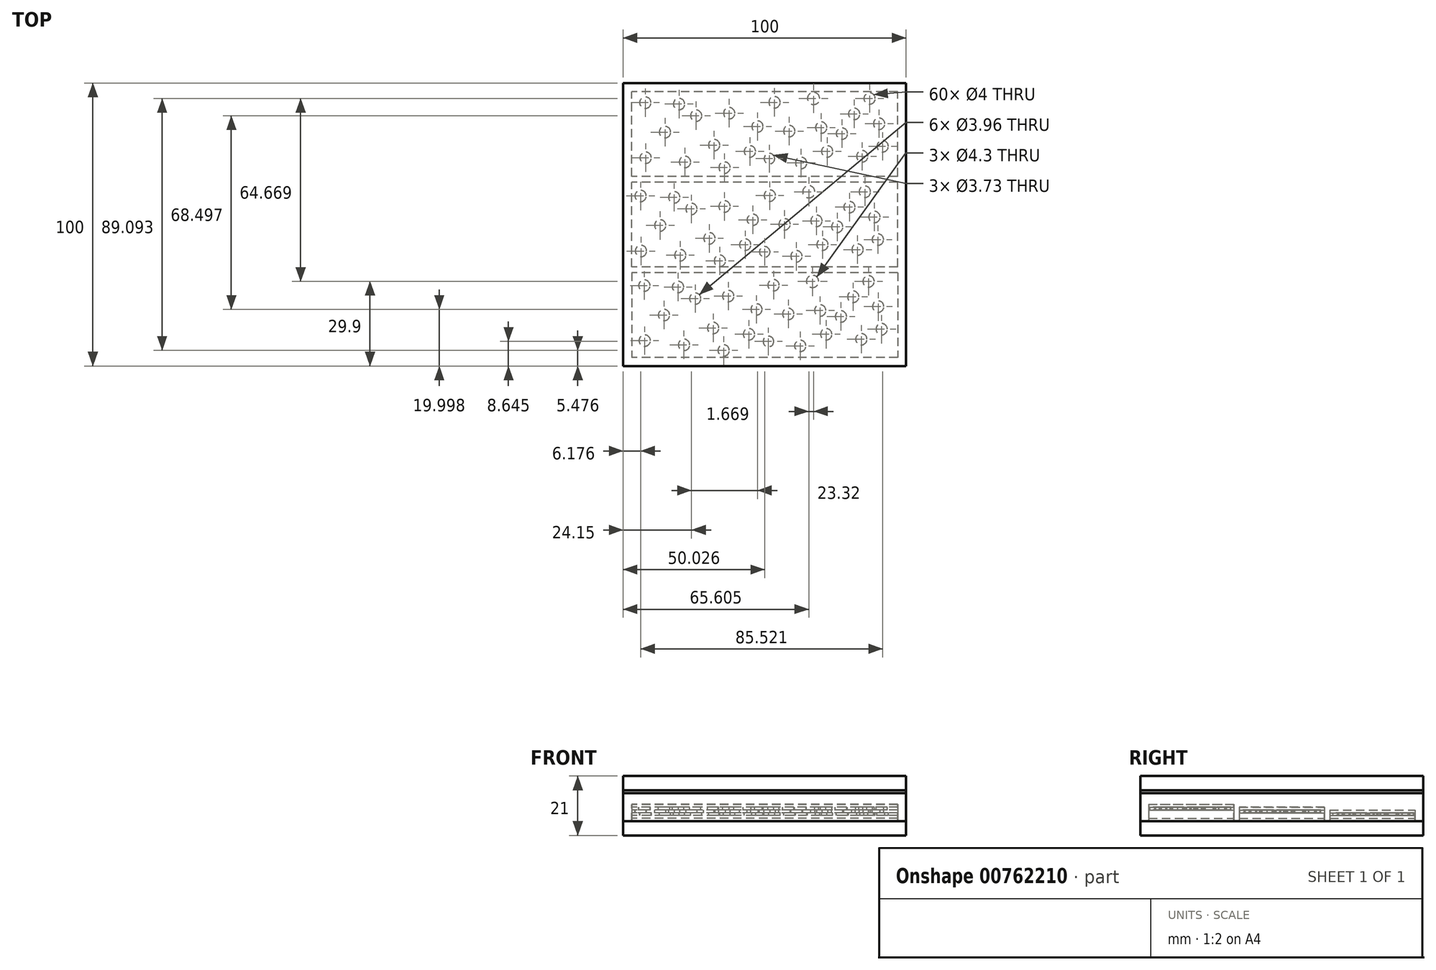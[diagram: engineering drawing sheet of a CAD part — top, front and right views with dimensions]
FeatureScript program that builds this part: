
annotation { "Feature Type Name" : "Feature", "Feature Type Description" : "" }
export const myFeature = defineFeature(function(context is Context, id is Id, definition is map)
    precondition{}
    {
        {
            var Q0;
            Q0=qCreatedBy(makeId("Top.planeOp"),FACE);
            var sketch = newSketch(context, id + "F0", { "sketchPlane" : qUnion([Q0])});
            skLineSegment(sketch, "E0.bottom", {"start": v(50, -50) * mm, "end": v(-50, -50) * mm});
            skLineSegment(sketch, "E0.top", {"start": v(50, 50) * mm, "end": v(-50, 50) * mm});
            skLineSegment(sketch, "E0.left", {"start": v(50, -50) * mm, "end": v(50, 50) * mm});
            skLineSegment(sketch, "E0.right", {"start": v(-50, -50) * mm, "end": v(-50, 50) * mm});
            skPoint(sketch, "E0.middle", {"position": v(0, 0) * mm});
            skSolve(sketch);
        }
        {
            var Q0;
            Q0=makeQuery(id+"F0.imprint","IMPRINT",FACE,{"disambiguationData":[TD([[makeQuery(id+"F0.imprint","IMPRINT",EDGE,{"derivedFrom":sQuery(id+"F0.wireOp",EDGE,"E0.bottom")}),-1.0]])]});
            extrude(context, id + "F1", {"entities" : qUnion([Q0]), "depth" : 5 * mm, "offsetDistance" : 25 * mm});
        }
        {
            var Q0;
            Q0=makeQuery(id+"F1.opExtrude","CAP_FACE",FACE,{"disambiguationData":[OSD([sQuery(id+"F0.wireOp",EDGE,"E0.bottom"),sQuery(id+"F0.wireOp",EDGE,"E0.top"),sQuery(id+"F0.wireOp",EDGE,"E0.left"),sQuery(id+"F0.wireOp",EDGE,"E0.right")])],"isStart":false});
            var sketch = newSketch(context, id + "F2", { "sketchPlane" : qUnion([Q0])});
            skLineSegment(sketch, "E1.bottom", {"start": v(47, -15) * mm, "end": v(-47, -15) * mm});
            skLineSegment(sketch, "E1.top", {"start": v(47, 15) * mm, "end": v(-47, 15) * mm});
            skLineSegment(sketch, "E1.left", {"start": v(47, -15) * mm, "end": v(47, 15) * mm});
            skLineSegment(sketch, "E1.right", {"start": v(-47, -15) * mm, "end": v(-47, 15) * mm});
            skPoint(sketch, "E1.middle", {"position": v(0, 0) * mm});
            skLineSegment(sketch, "E2.bottom", {"start": v(47, 17) * mm, "end": v(-47, 17) * mm});
            skLineSegment(sketch, "E2.top", {"start": v(47, 47) * mm, "end": v(-47, 47) * mm});
            skLineSegment(sketch, "E2.left", {"start": v(47, 17) * mm, "end": v(47, 47) * mm});
            skLineSegment(sketch, "E2.right", {"start": v(-47, 17) * mm, "end": v(-47, 47) * mm});
            skPoint(sketch, "E2.middle", {"position": v(0, 32) * mm});
            skLineSegment(sketch, "E3.bottom", {"start": v(47, -47) * mm, "end": v(-47, -47) * mm});
            skLineSegment(sketch, "E3.top", {"start": v(47, -17) * mm, "end": v(-47, -17) * mm});
            skLineSegment(sketch, "E3.left", {"start": v(47, -47) * mm, "end": v(47, -17) * mm});
            skLineSegment(sketch, "E3.right", {"start": v(-47, -47) * mm, "end": v(-47, -17) * mm});
            skPoint(sketch, "E3.middle", {"position": v(0, -32) * mm});
            skSolve(sketch);
        }
        {
            var Q0;
            Q0=makeQuery(id+"F2.imprint","IMPRINT",FACE,{"disambiguationData":[TD([[makeQuery(id+"F2.imprint","IMPRINT",EDGE,{"derivedFrom":sQuery(id+"F2.wireOp",EDGE,"E2.bottom")}),-1.0]])]});
            var Q1;
            Q1=makeQuery(id+"F2.imprint","IMPRINT",FACE,{"disambiguationData":[TD([[makeQuery(id+"F2.imprint","IMPRINT",EDGE,{"derivedFrom":sQuery(id+"F2.wireOp",EDGE,"E1.bottom")}),-1.0]])]});
            var Q2;
            Q2=makeQuery(id+"F2.imprint","IMPRINT",FACE,{"disambiguationData":[TD([[makeQuery(id+"F2.imprint","IMPRINT",EDGE,{"derivedFrom":sQuery(id+"F2.wireOp",EDGE,"E3.bottom")}),-1.0]])]});
            extrude(context, id + "F3", {"entities" : qUnion([Q0, Q1, Q2]), "depth" : 1 * mm, "offsetDistance" : 25 * mm});
        }
        {
            var Q0;
            Q0=makeQuery(id+"F3.opExtrude","CAP_FACE",FACE,{"disambiguationData":[OSD([sQuery(id+"F2.wireOp",EDGE,"E2.bottom"),sQuery(id+"F2.wireOp",EDGE,"E2.top"),sQuery(id+"F2.wireOp",EDGE,"E2.left"),sQuery(id+"F2.wireOp",EDGE,"E2.right")])],"isStart":false});
            extrude(context, id + "F4", {"entities" : qUnion([Q0]), "depth" : 1 * mm, "offsetDistance" : 25 * mm});
        }
        {
            var Q0;
            Q0=makeQuery(id+"F3.opExtrude","CAP_FACE",FACE,{"disambiguationData":[OSD([sQuery(id+"F2.wireOp",EDGE,"E1.bottom"),sQuery(id+"F2.wireOp",EDGE,"E1.top"),sQuery(id+"F2.wireOp",EDGE,"E1.left"),sQuery(id+"F2.wireOp",EDGE,"E1.right")])],"isStart":false});
            extrude(context, id + "F5", {"entities" : qUnion([Q0]), "depth" : 2 * mm, "offsetDistance" : 25 * mm});
        }
        {
            var Q0;
            Q0=makeQuery(id+"F3.opExtrude","CAP_FACE",FACE,{"disambiguationData":[OSD([sQuery(id+"F2.wireOp",EDGE,"E3.bottom"),sQuery(id+"F2.wireOp",EDGE,"E3.top"),sQuery(id+"F2.wireOp",EDGE,"E3.left"),sQuery(id+"F2.wireOp",EDGE,"E3.right")])],"isStart":false});
            extrude(context, id + "F6", {"entities" : qUnion([Q0]), "depth" : 3 * mm, "offsetDistance" : 25 * mm});
        }
        {
            var Q0;
            Q0=makeQuery(id+"F6.opExtrude","CAP_FACE",FACE,{"disambiguationData":[OSD([sQuery(id+"F2.wireOp",EDGE,"E3.bottom"),sQuery(id+"F2.wireOp",EDGE,"E3.top"),sQuery(id+"F2.wireOp",EDGE,"E3.left"),sQuery(id+"F2.wireOp",EDGE,"E3.right")])],"isStart":false});
            var Q1;
            Q1=makeQuery(id+"F5.opExtrude","CAP_FACE",FACE,{"disambiguationData":[OSD([sQuery(id+"F2.wireOp",EDGE,"E1.bottom"),sQuery(id+"F2.wireOp",EDGE,"E1.top"),sQuery(id+"F2.wireOp",EDGE,"E1.left"),sQuery(id+"F2.wireOp",EDGE,"E1.right")])],"isStart":false});
            var Q2;
            Q2=makeQuery(id+"F4.opExtrude","CAP_FACE",FACE,{"disambiguationData":[OSD([sQuery(id+"F2.wireOp",EDGE,"E2.bottom"),sQuery(id+"F2.wireOp",EDGE,"E2.top"),sQuery(id+"F2.wireOp",EDGE,"E2.left"),sQuery(id+"F2.wireOp",EDGE,"E2.right")])],"isStart":false});
            extrude(context, id + "F7", {"entities" : qUnion([Q0, Q1, Q2]), "depth" : 1 * mm, "offsetDistance" : 25 * mm});
        }
        {
            var Q0;
            Q0=makeQuery(id+"F7.opExtrude","CAP_FACE",FACE,{"disambiguationData":[OSD([sQuery(id+"F2.wireOp",EDGE,"E3.bottom"),sQuery(id+"F2.wireOp",EDGE,"E3.top"),sQuery(id+"F2.wireOp",EDGE,"E3.left"),sQuery(id+"F2.wireOp",EDGE,"E3.right")])],"isStart":false});
            var sketch = newSketch(context, id + "F8", { "sketchPlane" : qUnion([Q0])});
            skCircle(sketch, "E4", {"center": v(-35.55, -32) * mm, "radius": 2 * mm});
            skCircle(sketch, "E5", {"center": v(-18.19, -36.58) * mm, "radius": 2 * mm});
            skCircle(sketch, "E6", {"center": v(-12.85, -25.3) * mm, "radius": 2 * mm});
            skCircle(sketch, "E7", {"center": v(8.36, -31.62) * mm, "radius": 2 * mm});
            skCircle(sketch, "E8", {"center": v(19.64, -30.38) * mm, "radius": 2 * mm});
            skCircle(sketch, "E9", {"center": v(31.3, -25.54) * mm, "radius": 2 * mm});
            skCircle(sketch, "E10", {"center": v(34.16, -40.55) * mm, "radius": 2 * mm});
            skCircle(sketch, "E11", {"center": v(12.57, -42.9) * mm, "radius": 2 * mm});
            skCircle(sketch, "E12", {"center": v(3.15, -21.45) * mm, "radius": 2 * mm});
            skCircle(sketch, "E13", {"center": v(-5.53, -38.81) * mm, "radius": 2 * mm});
            skCircle(sketch, "E14", {"center": v(-30.59, -22.07) * mm, "radius": 2 * mm});
            skCircle(sketch, "E15", {"center": v(-42.37, -41.05) * mm, "radius": 2 * mm});
            skCircle(sketch, "E16", {"center": v(40.11, -29.01) * mm, "radius": 2 * mm});
            skCircle(sketch, "E17", {"center": v(-28.48, -42.53) * mm, "radius": 2 * mm});
            skCircle(sketch, "E18", {"center": v(21.75, -38.81) * mm, "radius": 2 * mm});
            skCircle(sketch, "E19", {"center": v(-42.5, -21.57) * mm, "radius": 2 * mm});
            skCircle(sketch, "E20", {"center": v(-2.87, -30) * mm, "radius": 1.98 * mm});
            skCircle(sketch, "E21", {"center": v(16.93, -20.1) * mm, "radius": 2.15 * mm});
            skCircle(sketch, "E22", {"center": v(-24.52, -26.17) * mm, "radius": 1.98 * mm});
            skCircle(sketch, "E23", {"center": v(36.73, -20.1) * mm, "radius": 2 * mm});
            skCircle(sketch, "E24", {"center": v(41.36, -37) * mm, "radius": 2 * mm});
            skCircle(sketch, "E25", {"center": v(26.97, -32.5) * mm, "radius": 2 * mm});
            skCircle(sketch, "E26", {"center": v(1.35, -41.36) * mm, "radius": 1.87 * mm});
            skCircle(sketch, "E27", {"center": v(-14.49, -44.52) * mm, "radius": 2 * mm});
            skSolve(sketch);
        }
        {
            var Q0;
            Q0 = qSketchRegion(id + "F8", true);
            extrude(context, id + "F9", {"entities" : qUnion([Q0]), "operationType" : NewBodyOperationType.REMOVE, "oppositeDirection" : true, "depth" : 1 * mm, "offsetDistance" : 25 * mm});
        }
        {
            var Q0;
            Q0=makeQuery(id+"F7.opExtrude","CAP_FACE",FACE,{"disambiguationData":[OSD([sQuery(id+"F2.wireOp",EDGE,"E1.bottom"),sQuery(id+"F2.wireOp",EDGE,"E1.top"),sQuery(id+"F2.wireOp",EDGE,"E1.left"),sQuery(id+"F2.wireOp",EDGE,"E1.right")])],"isStart":false});
            var sketch = newSketch(context, id + "F10", { "sketchPlane" : qUnion([Q0])});
            skCircle(sketch, "E28", {"center": v(-36.88, -0.3) * mm, "radius": 2 * mm});
            skCircle(sketch, "E29", {"center": v(-19.51, -4.9) * mm, "radius": 2 * mm});
            skCircle(sketch, "E30", {"center": v(-14.18, 6.4) * mm, "radius": 2 * mm});
            skCircle(sketch, "E31", {"center": v(7.03, 0.07) * mm, "radius": 2 * mm});
            skCircle(sketch, "E32", {"center": v(18.32, 1.3) * mm, "radius": 2 * mm});
            skCircle(sketch, "E33", {"center": v(29.98, 6.15) * mm, "radius": 2 * mm});
            skCircle(sketch, "E34", {"center": v(32.83, -8.86) * mm, "radius": 2 * mm});
            skCircle(sketch, "E35", {"center": v(11.25, -11.22) * mm, "radius": 2 * mm});
            skCircle(sketch, "E36", {"center": v(1.82, 10.24) * mm, "radius": 2 * mm});
            skCircle(sketch, "E37", {"center": v(-6.86, -7.13) * mm, "radius": 2 * mm});
            skCircle(sketch, "E38", {"center": v(-31.92, 9.62) * mm, "radius": 2 * mm});
            skCircle(sketch, "E39", {"center": v(-43.7, -9.36) * mm, "radius": 2 * mm});
            skCircle(sketch, "E40", {"center": v(38.78, 2.67) * mm, "radius": 2 * mm});
            skCircle(sketch, "E41", {"center": v(-29.8, -10.85) * mm, "radius": 2 * mm});
            skCircle(sketch, "E42", {"center": v(20.43, -7.13) * mm, "radius": 2 * mm});
            skCircle(sketch, "E43", {"center": v(-43.82, 10.12) * mm, "radius": 2 * mm});
            skCircle(sketch, "E44", {"center": v(-4.2, 1.69) * mm, "radius": 1.98 * mm});
            skCircle(sketch, "E45", {"center": v(15.6, 11.59) * mm, "radius": 2.15 * mm});
            skCircle(sketch, "E46", {"center": v(-25.85, 5.52) * mm, "radius": 1.98 * mm});
            skCircle(sketch, "E47", {"center": v(35.4, 11.59) * mm, "radius": 2 * mm});
            skCircle(sketch, "E48", {"center": v(40.03, -5.31) * mm, "radius": 2 * mm});
            skCircle(sketch, "E49", {"center": v(25.64, -0.82) * mm, "radius": 2 * mm});
            skCircle(sketch, "E50", {"center": v(0.03, -9.67) * mm, "radius": 1.87 * mm});
            skCircle(sketch, "E51", {"center": v(-15.82, -12.84) * mm, "radius": 2 * mm});
            skSolve(sketch);
        }
        {
            var Q0;
            Q0 = qSketchRegion(id + "F10", true);
            extrude(context, id + "F11", {"entities" : qUnion([Q0]), "operationType" : NewBodyOperationType.REMOVE, "oppositeDirection" : true, "depth" : 1 * mm, "offsetDistance" : 25 * mm});
        }
        {
            var Q0;
            Q0=makeQuery(id+"F7.opExtrude","CAP_FACE",FACE,{"disambiguationData":[OSD([sQuery(id+"F2.wireOp",EDGE,"E2.bottom"),sQuery(id+"F2.wireOp",EDGE,"E2.top"),sQuery(id+"F2.wireOp",EDGE,"E2.left"),sQuery(id+"F2.wireOp",EDGE,"E2.right")])],"isStart":false});
            var sketch = newSketch(context, id + "F12", { "sketchPlane" : qUnion([Q0])});
            skCircle(sketch, "E52", {"center": v(-35.2, 32.68) * mm, "radius": 2 * mm});
            skCircle(sketch, "E53", {"center": v(-17.84, 28.09) * mm, "radius": 2 * mm});
            skCircle(sketch, "E54", {"center": v(-12.51, 39.38) * mm, "radius": 2 * mm});
            skCircle(sketch, "E55", {"center": v(8.7, 33.05) * mm, "radius": 2 * mm});
            skCircle(sketch, "E56", {"center": v(19.99, 34.29) * mm, "radius": 2 * mm});
            skCircle(sketch, "E57", {"center": v(31.65, 39.13) * mm, "radius": 2 * mm});
            skCircle(sketch, "E58", {"center": v(34.5, 24.12) * mm, "radius": 2 * mm});
            skCircle(sketch, "E59", {"center": v(12.92, 21.76) * mm, "radius": 2 * mm});
            skCircle(sketch, "E60", {"center": v(3.49, 43.22) * mm, "radius": 2 * mm});
            skCircle(sketch, "E61", {"center": v(-5.2, 25.86) * mm, "radius": 2 * mm});
            skCircle(sketch, "E62", {"center": v(-30.25, 42.6) * mm, "radius": 2 * mm});
            skCircle(sketch, "E63", {"center": v(-42.03, 23.62) * mm, "radius": 2 * mm});
            skCircle(sketch, "E64", {"center": v(40.45, 35.65) * mm, "radius": 2 * mm});
            skCircle(sketch, "E65", {"center": v(-28.14, 22.13) * mm, "radius": 2 * mm});
            skCircle(sketch, "E66", {"center": v(22.1, 25.86) * mm, "radius": 2 * mm});
            skCircle(sketch, "E67", {"center": v(-42.16, 43.1) * mm, "radius": 2 * mm});
            skCircle(sketch, "E68", {"center": v(-2.53, 34.67) * mm, "radius": 1.98 * mm});
            skCircle(sketch, "E69", {"center": v(17.27, 44.57) * mm, "radius": 2.15 * mm});
            skCircle(sketch, "E70", {"center": v(-24.18, 38.5) * mm, "radius": 1.98 * mm});
            skCircle(sketch, "E71", {"center": v(37.08, 44.57) * mm, "radius": 2 * mm});
            skCircle(sketch, "E72", {"center": v(41.7, 27.67) * mm, "radius": 2 * mm});
            skCircle(sketch, "E73", {"center": v(27.3, 32.16) * mm, "radius": 2 * mm});
            skCircle(sketch, "E74", {"center": v(1.7, 23.31) * mm, "radius": 1.87 * mm});
            skCircle(sketch, "E75", {"center": v(-14.15, 20.14) * mm, "radius": 2 * mm});
            skSolve(sketch);
        }
        {
            var Q0;
            Q0 = qSketchRegion(id + "F12", true);
            extrude(context, id + "F13", {"entities" : qUnion([Q0]), "operationType" : NewBodyOperationType.REMOVE, "oppositeDirection" : true, "depth" : 1 * mm, "offsetDistance" : 25 * mm});
        }
        {
            var Q0;
            Q0=makeQuery(id+"F7.opExtrude","CAP_FACE",FACE,{"disambiguationData":[OSD([sQuery(id+"F2.wireOp",EDGE,"E2.bottom"),sQuery(id+"F2.wireOp",EDGE,"E2.top"),sQuery(id+"F2.wireOp",EDGE,"E2.left"),sQuery(id+"F2.wireOp",EDGE,"E2.right")])],"isStart":false});
            var sketch = newSketch(context, id + "F14", { "sketchPlane" : qUnion([Q0])});
            skLineSegment(sketch, "E76.bottom", {"start": v(47, 17) * mm, "end": v(-47, 17) * mm});
            skLineSegment(sketch, "E76.top", {"start": v(47, 47) * mm, "end": v(-47, 47) * mm});
            skLineSegment(sketch, "E76.left", {"start": v(47, 17) * mm, "end": v(47, 47) * mm});
            skLineSegment(sketch, "E76.right", {"start": v(-47, 17) * mm, "end": v(-47, 47) * mm});
            skPoint(sketch, "E76.middle", {"position": v(0, 32) * mm});
            skSolve(sketch);
        }
        {
            var Q0;
            Q0 = qSketchRegion(id + "F14", true);
            extrude(context, id + "F15", {"entities" : qUnion([Q0]), "depth" : 1 * mm, "offsetDistance" : 25 * mm});
        }
        {
            var Q0;
            Q0=makeQuery(id+"F7.opExtrude","CAP_FACE",FACE,{"disambiguationData":[OSD([sQuery(id+"F2.wireOp",EDGE,"E1.bottom"),sQuery(id+"F2.wireOp",EDGE,"E1.top"),sQuery(id+"F2.wireOp",EDGE,"E1.left"),sQuery(id+"F2.wireOp",EDGE,"E1.right")])],"isStart":false});
            var sketch = newSketch(context, id + "F16", { "sketchPlane" : qUnion([Q0])});
            skLineSegment(sketch, "E77.bottom", {"start": v(-47, -15) * mm, "end": v(47, -15) * mm});
            skLineSegment(sketch, "E77.top", {"start": v(-47, 15) * mm, "end": v(47, 15) * mm});
            skLineSegment(sketch, "E77.left", {"start": v(-47, -15) * mm, "end": v(-47, 15) * mm});
            skLineSegment(sketch, "E77.right", {"start": v(47, -15) * mm, "end": v(47, 15) * mm});
            skPoint(sketch, "E77.middle", {"position": v(0, 0) * mm});
            skSolve(sketch);
        }
        {
            var Q0;
            Q0 = qSketchRegion(id + "F16", true);
            extrude(context, id + "F17", {"entities" : qUnion([Q0]), "depth" : 1 * mm, "offsetDistance" : 25 * mm});
        }
        {
            var Q0;
            Q0=makeQuery(id+"F7.opExtrude","CAP_FACE",FACE,{"disambiguationData":[OSD([sQuery(id+"F2.wireOp",EDGE,"E3.bottom"),sQuery(id+"F2.wireOp",EDGE,"E3.top"),sQuery(id+"F2.wireOp",EDGE,"E3.left"),sQuery(id+"F2.wireOp",EDGE,"E3.right")])],"isStart":false});
            var sketch = newSketch(context, id + "F18", { "sketchPlane" : qUnion([Q0])});
            skLineSegment(sketch, "E78.bottom", {"start": v(47, -47) * mm, "end": v(-47, -47) * mm});
            skLineSegment(sketch, "E78.top", {"start": v(47, -17) * mm, "end": v(-47, -17) * mm});
            skLineSegment(sketch, "E78.left", {"start": v(47, -47) * mm, "end": v(47, -17) * mm});
            skLineSegment(sketch, "E78.right", {"start": v(-47, -47) * mm, "end": v(-47, -17) * mm});
            skPoint(sketch, "E78.middle", {"position": v(0, -32) * mm});
            skSolve(sketch);
        }
        {
            var Q0;
            Q0 = qSketchRegion(id + "F18", true);
            extrude(context, id + "F19", {"entities" : qUnion([Q0]), "depth" : 1 * mm, "offsetDistance" : 25 * mm});
        }
        {
            var Q0;
            Q0=makeQuery(id+"F15.opExtrude","SWEPT_FACE",FACE,{"disambiguationData":[OSD([sQuery(id+"F14.wireOp",EDGE,"E76.right")])]});
            var sketch = newSketch(context, id + "F20", { "sketchPlane" : qUnion([Q0])});
            skLineSegment(sketch, "E79", {"start": v(-50, 5) * mm, "end": v(-47, 5) * mm});
            skLineSegment(sketch, "E80", {"start": v(-47, 5) * mm, "end": v(-47, 8.94) * mm});
            skLineSegment(sketch, "E81", {"start": v(-47, 8.94) * mm, "end": v(-17, 8.94) * mm});
            skLineSegment(sketch, "E82", {"start": v(-17, 8.94) * mm, "end": v(-17, 5) * mm});
            skLineSegment(sketch, "E83", {"start": v(-17, 5) * mm, "end": v(-15, 5) * mm});
            skLineSegment(sketch, "E84", {"start": v(-15, 5) * mm, "end": v(-15, 10.02) * mm});
            skLineSegment(sketch, "E85", {"start": v(-15, 10.02) * mm, "end": v(15, 10.02) * mm});
            skLineSegment(sketch, "E86", {"start": v(15, 10.02) * mm, "end": v(15, 5) * mm});
            skLineSegment(sketch, "E87", {"start": v(15, 5) * mm, "end": v(17, 5) * mm});
            skLineSegment(sketch, "E88", {"start": v(17, 5) * mm, "end": v(17, 10.88) * mm});
            skLineSegment(sketch, "E89", {"start": v(17, 10.88) * mm, "end": v(47, 10.88) * mm});
            skLineSegment(sketch, "E90", {"start": v(47, 10.88) * mm, "end": v(47, 5) * mm});
            skLineSegment(sketch, "E91", {"start": v(47, 5) * mm, "end": v(50, 5) * mm});
            skLineSegment(sketch, "E92", {"start": v(50, 5) * mm, "end": v(50, 15) * mm});
            skLineSegment(sketch, "E93", {"start": v(50, 15) * mm, "end": v(-50, 15) * mm});
            skLineSegment(sketch, "E94", {"start": v(-50, 15) * mm, "end": v(-50, 5) * mm});
            skSolve(sketch);
        }
        {
            var Q0;
            {var subQ8=sQuery(id+"F20.wireOp",EDGE,"E79");Q0=makeQuery(id+"F20.imprint","IMPRINT",FACE,{"disambiguationData":[TD([[makeQuery(id+"F20.imprint","IMPRINT",EDGE,{"derivedFrom":subQ8}),1.0]])]});}
            extrude(context, id + "F21", {"entities" : qUnion([Q0]), "oppositeDirection" : true, "depth" : 94 * mm, "offsetDistance" : 25 * mm});
        }
        {
            var Q0;
            Q0=makeQuery(id+"F1.opExtrude","CAP_FACE",FACE,{"disambiguationData":[OSD([sQuery(id+"F0.wireOp",EDGE,"E0.bottom"),sQuery(id+"F0.wireOp",EDGE,"E0.top"),sQuery(id+"F0.wireOp",EDGE,"E0.left"),sQuery(id+"F0.wireOp",EDGE,"E0.right")])],"isStart":false});
            var sketch = newSketch(context, id + "F22", { "sketchPlane" : qUnion([Q0])});
            skLineSegment(sketch, "E95.bottom", {"start": v(-50, 50) * mm, "end": v(-47, 50) * mm});
            skLineSegment(sketch, "E95.top", {"start": v(-50, -50) * mm, "end": v(-47, -50) * mm});
            skLineSegment(sketch, "E95.left", {"start": v(-50, 50) * mm, "end": v(-50, -50) * mm});
            skLineSegment(sketch, "E95.right", {"start": v(-47, 50) * mm, "end": v(-47, -50) * mm});
            skLineSegment(sketch, "E96.bottom", {"start": v(47, 50) * mm, "end": v(50, 50) * mm});
            skLineSegment(sketch, "E96.top", {"start": v(47, -50) * mm, "end": v(50, -50) * mm});
            skLineSegment(sketch, "E96.left", {"start": v(47, 50) * mm, "end": v(47, -50) * mm});
            skLineSegment(sketch, "E96.right", {"start": v(50, 50) * mm, "end": v(50, -50) * mm});
            skSolve(sketch);
        }
        {
            var Q0;
            Q0=makeQuery(id+"F22.imprint","IMPRINT",FACE,{"disambiguationData":[TD([[makeQuery(id+"F22.imprint","IMPRINT",EDGE,{"derivedFrom":sQuery(id+"F22.wireOp",EDGE,"E95.bottom")}),1.0]])]});
            var Q1;
            Q1=makeQuery(id+"F22.imprint","IMPRINT",FACE,{"disambiguationData":[TD([[makeQuery(id+"F22.imprint","IMPRINT",EDGE,{"derivedFrom":sQuery(id+"F22.wireOp",EDGE,"E96.bottom")}),1.0]])]});
            extrude(context, id + "F23", {"entities" : qUnion([Q0, Q1]), "depth" : 10 * mm, "offsetDistance" : 25 * mm});
        }
        {
            var Q0;
            Q0=makeQuery(id+"F21.opExtrude","SWEPT_BODY",BODY,{"disambiguationData":[OSD([sQuery(id+"F14.wireOp",EDGE,"E76.bottom"),sQuery(id+"F14.wireOp",EDGE,"E76.top"),sQuery(id+"F14.wireOp",EDGE,"E76.right"),sQuery(id+"F20.wireOp",EDGE,"E79"),sQuery(id+"F20.wireOp",EDGE,"E80"),sQuery(id+"F20.wireOp",EDGE,"E82"),sQuery(id+"F20.wireOp",EDGE,"E83"),sQuery(id+"F20.wireOp",EDGE,"E84"),sQuery(id+"F20.wireOp",EDGE,"E85"),sQuery(id+"F20.wireOp",EDGE,"E86"),sQuery(id+"F20.wireOp",EDGE,"E87"),sQuery(id+"F20.wireOp",EDGE,"E88"),sQuery(id+"F20.wireOp",EDGE,"E89"),sQuery(id+"F20.wireOp",EDGE,"E90"),sQuery(id+"F20.wireOp",EDGE,"E91"),sQuery(id+"F20.wireOp",EDGE,"E92"),sQuery(id+"F20.wireOp",EDGE,"E93"),sQuery(id+"F20.wireOp",EDGE,"E94")])]});
            var Q1;
            Q1=makeQuery(id+"F23.opExtrude","SWEPT_BODY",BODY,{"disambiguationData":[OSD([sQuery(id+"F22.wireOp",EDGE,"E95.bottom"),sQuery(id+"F22.wireOp",EDGE,"E95.top"),sQuery(id+"F22.wireOp",EDGE,"E95.left"),sQuery(id+"F22.wireOp",EDGE,"E95.right")])]});
            var Q2;
            Q2=makeQuery(id+"F23.opExtrude","SWEPT_BODY",BODY,{"disambiguationData":[OSD([sQuery(id+"F22.wireOp",EDGE,"E96.bottom"),sQuery(id+"F22.wireOp",EDGE,"E96.top"),sQuery(id+"F22.wireOp",EDGE,"E96.left"),sQuery(id+"F22.wireOp",EDGE,"E96.right")])]});
            booleanBodies(context, id + "F24", {"operationType" : BooleanOperationType.UNION, "tools" : qUnion([Q0, Q1, Q2])});
        }
        {
            var Q0;
            Q0=makeQuery(id+"F24.opBoolean","MERGE",FACE,{"derivedFrom":[makeQuery(id+"F21.opExtrude","SWEPT_FACE",FACE,{"disambiguationData":[OSD([sQuery(id+"F20.wireOp",EDGE,"E93")])]}),makeQuery(id+"F23.opExtrude","CAP_FACE",FACE,{"disambiguationData":[OSD([sQuery(id+"F22.wireOp",EDGE,"E95.bottom"),sQuery(id+"F22.wireOp",EDGE,"E95.top"),sQuery(id+"F22.wireOp",EDGE,"E95.left"),sQuery(id+"F22.wireOp",EDGE,"E95.right")])],"isStart":false}),makeQuery(id+"F23.opExtrude","CAP_FACE",FACE,{"disambiguationData":[OSD([sQuery(id+"F22.wireOp",EDGE,"E96.bottom"),sQuery(id+"F22.wireOp",EDGE,"E96.top"),sQuery(id+"F22.wireOp",EDGE,"E96.left"),sQuery(id+"F22.wireOp",EDGE,"E96.right")])],"isStart":false})]});
            extrude(context, id + "F25", {"entities" : qUnion([Q0]), "depth" : 1 * mm, "offsetDistance" : 25 * mm});
        }
        {
            var Q0;
            Q0=makeQuery(id+"F25.opExtrude","CAP_FACE",FACE,{"disambiguationData":[OSD([sQuery(id+"F20.wireOp",EDGE,"E93"),sQuery(id+"F22.wireOp",EDGE,"E95.bottom"),sQuery(id+"F22.wireOp",EDGE,"E95.top"),sQuery(id+"F22.wireOp",EDGE,"E95.left"),sQuery(id+"F22.wireOp",EDGE,"E95.right"),sQuery(id+"F22.wireOp",EDGE,"E96.bottom"),sQuery(id+"F22.wireOp",EDGE,"E96.top"),sQuery(id+"F22.wireOp",EDGE,"E96.left"),sQuery(id+"F22.wireOp",EDGE,"E96.right")])],"isStart":false});
            extrude(context, id + "F26", {"entities" : qUnion([Q0]), "depth" : 5 * mm, "offsetDistance" : 25 * mm});
        }
    });
